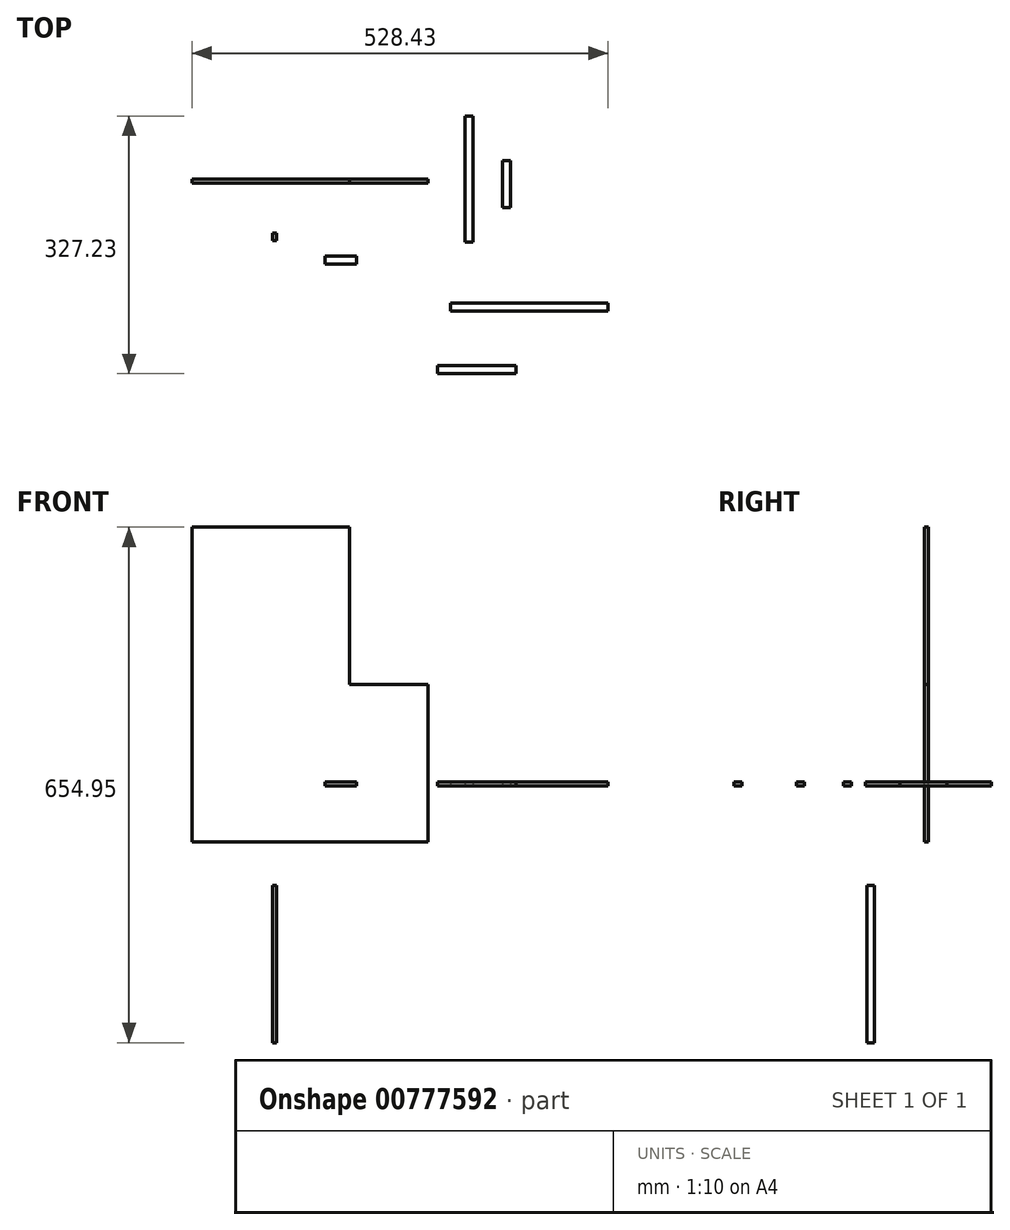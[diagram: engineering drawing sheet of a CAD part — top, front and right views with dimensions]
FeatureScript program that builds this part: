
annotation { "Feature Type Name" : "Feature", "Feature Type Description" : "" }
export const myFeature = defineFeature(function(context is Context, id is Id, definition is map)
    precondition{}
    {
        {
            var Q0;
            Q0=qCreatedBy(makeId("Front.planeOp"),FACE);
            var sketch = newSketch(context, id + "F0", { "sketchPlane" : qUnion([Q0])});
            skLineSegment(sketch, "E0", {"start": v(-102.46, 328.74) * mm, "end": v(97.54, 328.74) * mm});
            skLineSegment(sketch, "E1", {"start": v(-102.46, 328.74) * mm, "end": v(-102.46, -71.26) * mm});
            skLineSegment(sketch, "E2", {"start": v(-102.46, -71.26) * mm, "end": v(197.54, -71.26) * mm});
            skLineSegment(sketch, "E3", {"start": v(197.54, -71.26) * mm, "end": v(197.54, 128.74) * mm});
            skLineSegment(sketch, "E4", {"start": v(197.54, 128.74) * mm, "end": v(97.54, 128.74) * mm});
            skLineSegment(sketch, "E5", {"start": v(97.54, 128.74) * mm, "end": v(97.54, 328.74) * mm});
            skSolve(sketch);
        }
        {
            var Q0;
            Q0 = qSketchRegion(id + "F0", true);
            extrude(context, id + "F1", {"entities" : qUnion([Q0]), "depth" : 5 * mm, "offsetDistance" : 25 * mm});
        }
        {
            var Q0;
            Q0=qCreatedBy(makeId("Top.planeOp"),FACE);
            var sketch = newSketch(context, id + "F2", { "sketchPlane" : qUnion([Q0])});
            skLineSegment(sketch, "E6.bottom", {"start": v(254.45, -79.66) * mm, "end": v(244.45, -79.66) * mm});
            skLineSegment(sketch, "E6.top", {"start": v(254.45, 80.34) * mm, "end": v(244.45, 80.34) * mm});
            skLineSegment(sketch, "E6.left", {"start": v(254.45, -79.66) * mm, "end": v(254.45, 80.34) * mm});
            skLineSegment(sketch, "E6.right", {"start": v(244.45, -79.66) * mm, "end": v(244.45, 80.34) * mm});
            skLineSegment(sketch, "E7.bottom", {"start": v(106.35, -107.53) * mm, "end": v(66.35, -107.53) * mm});
            skLineSegment(sketch, "E7.top", {"start": v(106.35, -97.53) * mm, "end": v(66.35, -97.53) * mm});
            skLineSegment(sketch, "E7.left", {"start": v(106.35, -107.53) * mm, "end": v(106.35, -97.53) * mm});
            skLineSegment(sketch, "E7.right", {"start": v(66.35, -107.53) * mm, "end": v(66.35, -97.53) * mm});
            skLineSegment(sketch, "E8.bottom", {"start": v(302.34, -36) * mm, "end": v(292.34, -36) * mm});
            skLineSegment(sketch, "E8.top", {"start": v(302.34, 24) * mm, "end": v(292.34, 24) * mm});
            skLineSegment(sketch, "E8.left", {"start": v(302.34, -36) * mm, "end": v(302.34, 24) * mm});
            skLineSegment(sketch, "E8.right", {"start": v(292.34, -36) * mm, "end": v(292.34, 24) * mm});
            skLineSegment(sketch, "E9.bottom", {"start": v(425.97, -157.57) * mm, "end": v(225.97, -157.57) * mm});
            skLineSegment(sketch, "E9.top", {"start": v(425.97, -167.57) * mm, "end": v(225.97, -167.57) * mm});
            skLineSegment(sketch, "E9.left", {"start": v(425.97, -157.57) * mm, "end": v(425.97, -167.57) * mm});
            skLineSegment(sketch, "E9.right", {"start": v(225.97, -157.57) * mm, "end": v(225.97, -167.57) * mm});
            skLineSegment(sketch, "E10.bottom", {"start": v(309.27, -236.89) * mm, "end": v(209.27, -236.89) * mm});
            skLineSegment(sketch, "E10.top", {"start": v(309.27, -246.89) * mm, "end": v(209.27, -246.89) * mm});
            skLineSegment(sketch, "E10.left", {"start": v(309.27, -236.89) * mm, "end": v(309.27, -246.89) * mm});
            skLineSegment(sketch, "E10.right", {"start": v(209.27, -236.89) * mm, "end": v(209.27, -246.89) * mm});
            skSolve(sketch);
        }
        {
            var Q0;
            Q0=makeQuery(id+"F2.imprint","IMPRINT",FACE,{"disambiguationData":[TD([[makeQuery(id+"F2.imprint","IMPRINT",EDGE,{"derivedFrom":sQuery(id+"F2.wireOp",EDGE,"E9.bottom")}),1.0]])]});
            var Q1;
            Q1=makeQuery(id+"F2.imprint","IMPRINT",FACE,{"disambiguationData":[TD([[makeQuery(id+"F2.imprint","IMPRINT",EDGE,{"derivedFrom":sQuery(id+"F2.wireOp",EDGE,"E10.bottom")}),1.0]])]});
            var Q2;
            Q2=makeQuery(id+"F2.imprint","IMPRINT",FACE,{"disambiguationData":[TD([[makeQuery(id+"F2.imprint","IMPRINT",EDGE,{"derivedFrom":sQuery(id+"F2.wireOp",EDGE,"E7.bottom")}),-1.0]])]});
            var Q3;
            Q3=makeQuery(id+"F2.imprint","IMPRINT",FACE,{"disambiguationData":[TD([[makeQuery(id+"F2.imprint","IMPRINT",EDGE,{"derivedFrom":sQuery(id+"F2.wireOp",EDGE,"E6.bottom")}),-1.0]])]});
            var Q4;
            Q4=makeQuery(id+"F2.imprint","IMPRINT",FACE,{"disambiguationData":[TD([[makeQuery(id+"F2.imprint","IMPRINT",EDGE,{"derivedFrom":sQuery(id+"F2.wireOp",EDGE,"E8.bottom")}),-1.0]])]});
            extrude(context, id + "F3", {"entities" : qUnion([Q0, Q1, Q2, Q3, Q4]), "operationType" : NewBodyOperationType.ADD, "depth" : 5 * mm, "offsetDistance" : 25 * mm});
        }
        {
            var Q0;
            Q0=qCreatedBy(makeId("Right.planeOp"),FACE);
            var sketch = newSketch(context, id + "F4", { "sketchPlane" : qUnion([Q0])});
            skLineSegment(sketch, "E11", {"start": v(-68.2, -326.21) * mm, "end": v(-78.2, -326.21) * mm});
            skLineSegment(sketch, "E12", {"start": v(-78.2, -326.21) * mm, "end": v(-78.2, -276.21) * mm});
            skLineSegment(sketch, "E13", {"start": v(-78.2, -276.21) * mm, "end": v(-68.2, -276.21) * mm});
            skLineSegment(sketch, "E14", {"start": v(-68.2, -276.21) * mm, "end": v(-68.2, -226.21) * mm});
            skLineSegment(sketch, "E15", {"start": v(-68.2, -226.21) * mm, "end": v(-78.2, -226.21) * mm});
            skLineSegment(sketch, "E16", {"start": v(-78.2, -226.21) * mm, "end": v(-78.2, -176.21) * mm});
            skLineSegment(sketch, "E17", {"start": v(-78.2, -176.21) * mm, "end": v(-68.2, -176.21) * mm});
            skLineSegment(sketch, "E18", {"start": v(-68.2, -176.21) * mm, "end": v(-68.2, -126.21) * mm});
            skLineSegment(sketch, "E19", {"start": v(-68.2, -126.21) * mm, "end": v(-78.2, -126.21) * mm});
            skLineSegment(sketch, "E20", {"start": v(-78.2, -126.21) * mm, "end": v(-78.2, -176.21) * mm});
            skLineSegment(sketch, "E21", {"start": v(-68.2, -176.21) * mm, "end": v(-68.2, -226.21) * mm});
            skLineSegment(sketch, "E22", {"start": v(-78.2, -226.21) * mm, "end": v(-78.2, -276.21) * mm});
            skLineSegment(sketch, "E23", {"start": v(-68.2, -326.21) * mm, "end": v(-68.2, -276.21) * mm});
            skSolve(sketch);
        }
        {
            var Q0;
            Q0=makeQuery(id+"F4.imprint","IMPRINT",FACE,{"disambiguationData":[TD([[makeQuery(id+"F4.imprint","IMPRINT",EDGE,{"derivedFrom":sQuery(id+"F4.wireOp",EDGE,"E11")}),-1.0]])]});
            var Q1;
            Q1=makeQuery(id+"F4.imprint","IMPRINT",FACE,{"disambiguationData":[TD([[makeQuery(id+"F4.imprint","IMPRINT",EDGE,{"derivedFrom":sQuery(id+"F4.wireOp",EDGE,"E13")}),1.0]])]});
            var Q2;
            Q2=makeQuery(id+"F4.imprint","IMPRINT",FACE,{"disambiguationData":[TD([[makeQuery(id+"F4.imprint","IMPRINT",EDGE,{"derivedFrom":sQuery(id+"F4.wireOp",EDGE,"E15")}),-1.0]])]});
            var Q3;
            Q3=makeQuery(id+"F4.imprint","IMPRINT",FACE,{"disambiguationData":[TD([[makeQuery(id+"F4.imprint","IMPRINT",EDGE,{"derivedFrom":sQuery(id+"F4.wireOp",EDGE,"E17")}),1.0]])]});
            extrude(context, id + "F5", {"entities" : qUnion([Q0, Q1, Q2, Q3]), "depth" : 5 * mm, "offsetDistance" : 25 * mm});
        }
    });
